FCSTD DOCUMENT  (FreeCAD 2023.521R14555 (Git shallow))
Label: Lens_asm
License: All rights reserved
objects: App::Link×4, App::DocumentObjectGroup×3, PartDesign::CoordinateSystem×1, App::FeaturePython×1, App::Part×1
note: 1 computed .brp shape members not serialized (recipe doc carries the construction recipe); baked Part::Feature solids carry a one-line shape summary decoded from their .brp
EXTERNAL_REF file=Lens_mount.FCStd obj=Local_CS
EXTERNAL_REF file=Lens_mount.FCStd obj=Part
EXTERNAL_REF file=Lens_clamp.FCStd obj=Local_CS
EXTERNAL_REF file=Lens_mount.FCStd obj=Local_CS001
EXTERNAL_REF file=Lens_clamp.FCStd obj=Part
EXTERNAL_REF file=Light_mount.FCStd obj=LCS_0
EXTERNAL_REF file=Light_mount.FCStd obj=Light_mount
EXTERNAL_REF file=Lens_Filter.FCStd obj=Local_CS
EXTERNAL_REF file=Light_mount.FCStd obj=Local_CS
EXTERNAL_REF file=Lens_Filter.FCStd obj=Part

FEATURE [App::DocumentObjectGroup] Parts
  ClaimAllChildren = true
  ExportMode = 1
  TreeRank = 12
  _GroupVersion = 1
FEATURE [PartDesign::CoordinateSystem] LCS_Origin
  AttacherType = Attacher::AttachEngine3D
  AttachmentSupport = -> [X_Axis]
  InvalidShape = false
  MapMode = 2
  Support = -> [X_Axis]
  TreeRank = 4
  ValidateShape = false
FEATURE [App::DocumentObjectGroup] Constraints
  ClaimAllChildren = true
  ExportMode = 1
  TreeRank = 11
  _GroupVersion = 1
FEATURE [App::FeaturePython] Variables  # WARN: FeaturePython — macro-defined, semantics opaque (R4)
  TreeRank = 17
  Type = App::PropertyContainer
FEATURE [App::DocumentObjectGroup] Configurations
  ClaimAllChildren = true
  ExportMode = 1
  TreeRank = 18
  _GroupVersion = 1
FEATURE [App::Link] Mount  label="Mount(Mount)"
  AttachedBy = #Local_CS
  AttachedTo = Parent Assembly#LCS_Origin
  AutoLinkLabel = true
  AutoPlacement = true
  LinkedObject = -> <external Lens_mount.FCStd>#Part
  SolverId = Asm4EE
  SyncGroupVisibility = false
  TreeRank = 19
  _LinkVersion = 1
  expr: Placement = LCS_Origin.Placement * AttachmentOffset * Lens_mount#Local_CS.Placement ^ (-1)
FEATURE [App::Link] Clamp  label="Clamp(Clamp)"
  AttachedBy = #Local_CS
  AttachedTo = Mount#Local_CS001
  AutoLinkLabel = true
  AutoPlacement = true
  LinkPlacement = pos=(9.2457e-12,0.0015863,67) rot=(0,0,1;4.71239rad)
  LinkedObject = -> <external Lens_clamp.FCStd>#Part
  Placement = pos=(9.2457e-12,0.0015863,67) rot=(0,0,1;4.71239rad)
  SolverId = Asm4EE
  SyncGroupVisibility = false
  TreeRank = 20
  _LinkVersion = 1
  expr: Placement = Mount.Placement * Lens_mount#Local_CS001.Placement * AttachmentOffset * Lens_clamp#Local_CS.Placement ^ (-1)
FEATURE [App::Link] Light_mount  label="Light_mount(Light_mount)"
  AttachedBy = #LCS_0
  AttachedTo = Mount#Local_CS001
  AttachmentOffset = pos=(0,0,0) rot=(0,0,1;3.14159rad)
  AutoLinkLabel = true
  AutoPlacement = true
  LinkPlacement = pos=(9.2452e-12,0.0015863,65) rot=(0,0,1;0rad)
  LinkedObject = -> <external Light_mount.FCStd>#Light_mount
  Placement = pos=(9.2452e-12,0.0015863,65) rot=(0,0,1;0rad)
  SolverId = Asm4EE
  SyncGroupVisibility = false
  TreeRank = 21
  _LinkVersion = 1
  expr: Placement = Mount.Placement * Lens_mount#Local_CS001.Placement * AttachmentOffset * Light_mount#LCS_0.Placement ^ (-1)
FEATURE [App::Link] Filter001  label="Filter001(Filter001)"
  AttachedBy = #Local_CS
  AttachedTo = Light_mount#Local_CS
  AttachmentOffset = pos=(0,0,0) rot=(0,0,1;4.71239rad)
  AutoLinkLabel = true
  AutoPlacement = true
  LinkPlacement = pos=(9.251e-12,-64.9984,87.5) rot=(0,0,1;0rad)
  LinkedObject = -> <external Lens_Filter.FCStd>#Part
  Placement = pos=(9.251e-12,-64.9984,87.5) rot=(0,0,1;0rad)
  SolverId = Asm4EE
  SyncGroupVisibility = false
  TreeRank = 22
  _LinkVersion = 1
  expr: Placement = Light_mount.Placement * Light_mount#Local_CS.Placement * AttachmentOffset * Lens_Filter#Local_CS.Placement ^ (-1)
FEATURE [App::Part] Assembly
  AssemblyType = Part::Link
  ClaimAllChildren = false
  ExportMode = 1
  Group = -> [LCS_Origin,Constraints,Variables,Configurations,Mount,Clamp,Light_mount,Filter001]
  Origin = -> Origin
  TreeRank = 14
  Type = Assembly
  _ExportChildren = -> [LCS_Origin,Constraints,Variables,Configurations,Mount,Clamp,Light_mount,Filter001]
  _GroupVersion = 1

RESOLVED EXTERNAL PARTS (link-assembly join: the EXTERNAL_REF files above that resolve inside this repo's crawl, each included once):
---- part Lens_Filter.FCStd = doc fcstd_d97ffb5e31ca ----
FCSTD DOCUMENT  (FreeCAD 2023.521R14555 (Git shallow))
Label: Lens_Filter
License: All rights reserved
objects: Sketcher::SketchObject×4, PartDesign::Pad×2, PartDesign::Pocket×2, PartDesign::Chamfer×1, PartDesign::Body×1, PartDesign::CoordinateSystem×1, App::Part×1
note: 25 computed .brp shape members not serialized (recipe doc carries the construction recipe); baked Part::Feature solids carry a one-line shape summary decoded from their .brp

FEATURE [Sketcher::SketchObject] Sketch
  ArcFitTolerance = 1e-06
  AttachmentSupport = -> [XZ_Plane]
  ExternalBSplineMaxDegree = 5
  ExternalBSplineTolerance = 0.0001
  FullyConstrained = true
  InternalTolerance = 1e-06
  InvalidShape = false
  MakeInternals = false
  MapMode = 5
  Placement = pos=(0,0,0) rot=(1,0,0;1.5708rad)
  Support = -> [XZ_Plane]
  TreeRank = 14
  ValidateShape = false
  sketch-geometry (5):
    g0: LineSegment StartX=-44.5 StartY=-2.25 StartZ=0 EndX=-44.5 EndY=2.25 EndZ=0
    g1: LineSegment StartX=-44.5 StartY=2.25 StartZ=0 EndX=44.5 EndY=2.25 EndZ=0
    g2: LineSegment StartX=44.5 StartY=2.25 StartZ=0 EndX=44.5 EndY=-2.25 EndZ=0
    g3: LineSegment StartX=44.5 StartY=-2.25 StartZ=0 EndX=-44.5 EndY=-2.25 EndZ=0
    g4: GeomPoint [constr] X=0 Y=0 Z=0
  constraints (12):
    c: Coincident(g0,g1)
    c: Coincident(g1,g2)
    c: Coincident(g2,g3)
    c: Coincident(g3,g0)
    c: Horizontal(g1)
    c: Horizontal(g3)
    c: Vertical(g0)
    c: Vertical(g2)
    c: Symmetric(g1,g0,g4)
    c: Coincident(g4,g-1)
    c: DistanceX(g1,g1) = 89
    c: DistanceY(g2,g2) = 4.5
FEATURE [PartDesign::Pad] Pad
  AddSubType = 0
  AlongSketchNormal = false
  AutoTaperInnerAngle = true
  CheckUpToFaceLimits = true
  ClaimChildren = false
  Direction = (0,-1,-2e-16)
  Fit = 0
  FitJoin = 0
  InnerFit = 0
  InnerFitJoin = 0
  InvalidShape = false
  Length = 125
  Length2 = 10
  Linearize = true
  NewSolid = false
  Profile = -> Sketch
  ReferenceAxis = -> Sketch [N_Axis]
  Reversed = true
  Suppress = false
  TaperInnerAngle = 0
  TaperInnerAngleRev = 0
  TreeRank = 15
  Type = 0
  ValidateShape = true
  _ProfileBasedVersion = 1
FEATURE [Sketcher::SketchObject] Sketch001
  ArcFitTolerance = 1e-06
  AttachmentSupport = -> [Pad]
  ExternalBSplineMaxDegree = 5
  ExternalBSplineTolerance = 0.0001
  FullyConstrained = true
  InternalTolerance = 1e-06
  InvalidShape = false
  MakeInternals = false
  MapMode = 5
  Placement = pos=(0,-5e-16,2.25) rot=(0,0,1;0rad)
  Support = -> [Pad]
  TreeRank = 16
  ValidateShape = false
  sketch-geometry (5):
    g0: LineSegment StartX=-38.25 StartY=104 StartZ=0 EndX=-38.25 EndY=27.5 EndZ=0
    g1: LineSegment StartX=-38.25 StartY=27.5 StartZ=0 EndX=38.25 EndY=27.5 EndZ=0
    g2: LineSegment StartX=38.25 StartY=27.5 StartZ=0 EndX=38.25 EndY=104 EndZ=0
    g3: LineSegment StartX=38.25 StartY=104 StartZ=0 EndX=-38.25 EndY=104 EndZ=0
    g4: GeomPoint [constr] X=0 Y=65.75 Z=0
  constraints (13):
    c: Coincident(g0,g1)
    c: Coincident(g1,g2)
    c: Coincident(g2,g3)
    c: Coincident(g3,g0)
    c: Horizontal(g1)
    c: Horizontal(g3)
    c: Vertical(g0)
    c: Vertical(g2)
    c: Symmetric(g1,g0,g4)
    c: Vertical(g4,g-1)
    c: DistanceY(g2,g2) = 76.5
    c: Equal(g2,g3)
    c: DistanceY(g-1,g0) = 27.5
FEATURE [PartDesign::Pocket] Pocket
  AddSubType = 1
  AlongSketchNormal = false
  AutoTaperInnerAngle = true
  BaseFeature = -> Pad
  CheckUpToFaceLimits = true
  ClaimChildren = false
  Direction = (0,2e-16,-1)
  Fit = 0
  FitJoin = 0
  InnerFit = 0
  InnerFitJoin = 0
  InvalidShape = false
  Length = 0
  Length2 = 10
  Linearize = true
  NewSolid = false
  Offset = -1
  Profile = -> Sketch001
  ReferenceAxis = -> Sketch001 [N_Axis]
  Suppress = false
  TaperInnerAngle = 0
  TaperInnerAngleRev = 0
  TreeRank = 17
  Type = 3
  UpToFace = -> Pad [Face4]
  ValidateShape = true
  _ProfileBasedVersion = 1
  _Version = 1
FEATURE [Sketcher::SketchObject] Sketch002
  ArcFitTolerance = 1e-06
  AttachmentSupport = -> [Pocket]
  ExternalBSplineMaxDegree = 5
  ExternalBSplineTolerance = 0.0001
  ExternalGeometry = -> [Pocket]
  FullyConstrained = true
  InternalTolerance = 1e-06
  InvalidShape = false
  MakeInternals = false
  MapMode = 5
  Placement = pos=(0,3e-16,-1.25) rot=(0,0,1;0rad)
  Support = -> [Pocket]
  TreeRank = 18
  ValidateShape = false
  sketch-geometry (5):
    g0: LineSegment StartX=-35 StartY=30.75 StartZ=0 EndX=-35 EndY=100.75 EndZ=0
    g1: LineSegment StartX=-35 StartY=100.75 StartZ=0 EndX=35 EndY=100.75 EndZ=0
    g2: LineSegment StartX=35 StartY=100.75 StartZ=0 EndX=35 EndY=30.75 EndZ=0
    g3: LineSegment StartX=35 StartY=30.75 StartZ=0 EndX=-35 EndY=30.75 EndZ=0
    g4: GeomPoint [constr] X=4e-16 Y=65.75 Z=0
  constraints (12):
    c: Coincident(g0,g1)
    c: Coincident(g1,g2)
    c: Coincident(g2,g3)
    c: Coincident(g3,g0)
    c: Horizontal(g1)
    c: Horizontal(g3)
    c: Vertical(g0)
    c: Vertical(g2)
    c: Symmetric(g1,g0,g4)
    c: Symmetric(g-3,g-4,g4)
    c: Equal(g2,g1)
    c: DistanceY(g2,g2) = 70
FEATURE [PartDesign::Pocket] Pocket001
  AddSubType = 1
  AlongSketchNormal = false
  AutoTaperInnerAngle = true
  BaseFeature = -> Pocket
  CheckUpToFaceLimits = true
  ClaimChildren = false
  Direction = (0,2e-16,-1)
  Fit = 0
  FitJoin = 0
  InnerFit = 0
  InnerFitJoin = 0
  InvalidShape = false
  Length = 5
  Length2 = 10
  Linearize = true
  Midplane = true
  NewSolid = false
  Profile = -> Sketch002
  ReferenceAxis = -> Sketch002 [N_Axis]
  Suppress = false
  TaperInnerAngle = 0
  TaperInnerAngleRev = 0
  TreeRank = 19
  Type = 1
  ValidateShape = true
  _ProfileBasedVersion = 1
  _Version = 1
FEATURE [Sketcher::SketchObject] Sketch003
  ArcFitTolerance = 1e-06
  AttachmentSupport = -> [Pocket001]
  ExternalBSplineMaxDegree = 5
  ExternalBSplineTolerance = 0.0001
  ExternalGeometry = -> [Pocket001]
  FullyConstrained = true
  InternalTolerance = 1e-06
  InvalidShape = false
  MakeInternals = false
  MapMode = 5
  Placement = pos=(0,0,0) rot=(1,0,0;1.5708rad)
  Support = -> [Pocket001]
  TreeRank = 20
  ValidateShape = false
  sketch-geometry (5):
    g0: LineSegment StartX=-44.5 StartY=12.75 StartZ=0 EndX=-44.5 EndY=-2.25 EndZ=0
    g1: LineSegment StartX=-44.5 StartY=-2.25 StartZ=0 EndX=44.5 EndY=-2.25 EndZ=0
    g2: LineSegment StartX=44.5 StartY=-2.25 StartZ=0 EndX=44.5 EndY=12.75 EndZ=0
    g3: LineSegment StartX=44.5 StartY=12.75 StartZ=0 EndX=-44.5 EndY=12.75 EndZ=0
    g4: GeomPoint [constr] X=0 Y=5.25 Z=0
  constraints (12):
    c: Coincident(g0,g1)
    c: Coincident(g1,g2)
    c: Coincident(g2,g3)
    c: Coincident(g3,g0)
    c: Horizontal(g1)
    c: Horizontal(g3)
    c: Vertical(g0)
    c: Vertical(g2)
    c: Symmetric(g1,g0,g4)
    c: PointOnObject(g4,g-2)
    c: Coincident(g0,g-3)
    c: DistanceY(g2,g2) = 15
FEATURE [PartDesign::Pad] Pad001
  AddSubType = 0
  AlongSketchNormal = false
  AutoTaperInnerAngle = true
  BaseFeature = -> Pocket001
  CheckUpToFaceLimits = true
  ClaimChildren = false
  Direction = (0,-1,-2e-16)
  Fit = 0
  FitJoin = 0
  InnerFit = 0
  InnerFitJoin = 0
  InvalidShape = false
  Length = 5
  Length2 = 10
  Linearize = true
  NewSolid = false
  Profile = -> Sketch003
  ReferenceAxis = -> Sketch003 [N_Axis]
  Suppress = false
  TaperInnerAngle = 0
  TaperInnerAngleRev = 0
  TreeRank = 21
  Type = 0
  ValidateShape = true
  _ProfileBasedVersion = 1
FEATURE [PartDesign::Chamfer] Chamfer
  AddSubType = 0
  Angle = 45
  Base = -> Pad001 [Edge46,Edge45,Edge36,Edge19,Edge22,Edge47]
  BaseFeature = -> Pad001
  ChamferType = 0
  FlipDirection = false
  InvalidShape = false
  NewSolid = false
  Size = 2
  Size2 = 1
  SupportTransform = false
  Suppress = false
  TreeRank = 22
  UseAllEdges = false
  ValidateShape = true
FEATURE [PartDesign::Body] Body
  AutoGroupSolids = false
  ClaimAllChildren = false
  ExportMode = 0
  Group = -> [Sketch,Pad,Sketch001,Pocket,Sketch002,Pocket001,Sketch003,Pad001,Chamfer]
  InvalidShape = false
  Origin = -> Origin001
  Tip = -> Chamfer
  TreeRank = 13
  ValidateShape = false
  _ExportChildren = -> [Pad,Pocket,Pocket001,Pad001,Chamfer]
  _GroupVersion = 1
FEATURE [PartDesign::CoordinateSystem] Local_CS  label="Filter"
  AttacherType = Attacher::AttachEngine3D
  AttachmentSupport = -> [Chamfer]
  InvalidShape = false
  MapMode = 5
  Placement = pos=(0,125,2.78e-14) rot=(0,0.707107,0.707107;3.14159rad)
  Support = -> [Chamfer]
  TreeRank = 23
  ValidateShape = false
FEATURE [App::Part] Part  label="Filter001"
  ClaimAllChildren = false
  ExportMode = 1
  Group = -> [Body,Local_CS]
  Origin = -> Origin
  TreeRank = 3
  _ExportChildren = -> [Body,Local_CS]
  _GroupVersion = 1
---- part Lens_clamp.FCStd = doc fcstd_ed5a11fa4ce1 ----
FCSTD DOCUMENT  (FreeCAD 2023.521R14555 (Git shallow))
Label: Lens_clamp
License: All rights reserved
objects: Sketcher::SketchObject×3, PartDesign::Pad×1, PartDesign::Groove×1, PartDesign::CoordinateSystem×1, PartDesign::Pocket×1, PartDesign::Fillet×1, PartDesign::Body×1, App::Part×1
note: 20 computed .brp shape members not serialized (recipe doc carries the construction recipe); baked Part::Feature solids carry a one-line shape summary decoded from their .brp

FEATURE [Sketcher::SketchObject] Sketch
  ArcFitTolerance = 1e-06
  AttachmentSupport = -> [XY_Plane]
  ExternalBSplineMaxDegree = 5
  ExternalBSplineTolerance = 0.0001
  FullyConstrained = true
  InternalTolerance = 1e-06
  InvalidShape = false
  MakeInternals = false
  MapMode = 5
  Support = -> [XY_Plane]
  TreeRank = 12
  ValidateShape = false
  sketch-geometry (7):
    g0: Circle CenterX=-55 CenterY=55 CenterZ=0 NormalX=0 NormalY=0 NormalZ=1 AngleXU=0 Radius=2.75
    g1: Circle CenterX=55 CenterY=55 CenterZ=0 NormalX=0 NormalY=0 NormalZ=1 AngleXU=0 Radius=2.75
    g2: Circle CenterX=55 CenterY=-55 CenterZ=0 NormalX=0 NormalY=0 NormalZ=1 AngleXU=0 Radius=2.75
    g3: Circle CenterX=-55 CenterY=-55 CenterZ=0 NormalX=0 NormalY=0 NormalZ=1 AngleXU=0 Radius=2.75
    g4: Circle CenterX=0 CenterY=0 CenterZ=0 NormalX=0 NormalY=0 NormalZ=1 AngleXU=0 Radius=85
    g5: LineSegment [constr] StartX=0 StartY=0 StartZ=0 EndX=55 EndY=55 EndZ=0
    g6: LineSegment [constr] StartX=0 StartY=0 StartZ=0 EndX=55 EndY=-55 EndZ=0
  constraints (16):
    c: Equal(g2,g1)
    c: Equal(g1,g0)
    c: Equal(g0,g3)
    c: Diameter(g3) = 5.5
    c: Coincident(g4,g-1)
    c: Diameter(g4) = 170
    c: Coincident(g5,g4)
    c: Coincident(g5,g1)
    c: Coincident(g6,g4)
    c: Coincident(g6,g2)
    c: Equal(g6,g5)
    c: DistanceX(g6,g6) = 55
    c: Symmetric(g2,g0,g4)
    c: Symmetric(g3,g1,g4)
    c: Perpendicular(g5,g6)
    c: Vertical(g2,g1)
FEATURE [PartDesign::Pad] Pad
  AddSubType = 0
  AlongSketchNormal = false
  AutoTaperInnerAngle = true
  CheckUpToFaceLimits = true
  ClaimChildren = false
  Direction = (0,0,1)
  Fit = 0
  FitJoin = 0
  InnerFit = 0
  InnerFitJoin = 0
  InvalidShape = false
  Length = 20
  Length2 = 10
  Linearize = true
  NewSolid = false
  Profile = -> Sketch
  ReferenceAxis = -> Sketch [N_Axis]
  Reversed = true
  Suppress = false
  TaperInnerAngle = 0
  TaperInnerAngleRev = 0
  TreeRank = 13
  Type = 0
  ValidateShape = true
  _ProfileBasedVersion = 1
FEATURE [Sketcher::SketchObject] Sketch001
  ArcFitTolerance = 1e-06
  AttachmentSupport = -> [XZ_Plane]
  ExternalBSplineMaxDegree = 5
  ExternalBSplineTolerance = 0.0001
  ExternalGeometry = -> [Pad]
  FullyConstrained = true
  InternalTolerance = 1e-06
  InvalidShape = false
  MakeInternals = false
  MapMode = 5
  Placement = pos=(0,0,0) rot=(1,0,0;1.5708rad)
  Support = -> [XZ_Plane]
  TreeRank = 14
  ValidateShape = false
  sketch-geometry (8):
    g0: LineSegment StartX=-70 StartY=-2 StartZ=0 EndX=-85 EndY=-2 EndZ=0
    g1: LineSegment StartX=-85 StartY=-2 StartZ=0 EndX=-85 EndY=-20 EndZ=0
    g2: LineSegment StartX=-85 StartY=-20 StartZ=0 EndX=0 EndY=-20 EndZ=0
    g3: LineSegment StartX=0 StartY=-20 StartZ=0 EndX=0 EndY=0 EndZ=0
    g4: LineSegment StartX=0 StartY=0 StartZ=0 EndX=-65.8 EndY=0 EndZ=0
    g5: LineSegment StartX=-61 StartY=-12 StartZ=0 EndX=-55 EndY=-12 EndZ=0
    g6: LineSegment StartX=-70 StartY=-2 StartZ=0 EndX=-61 EndY=-12 EndZ=0
    g7: LineSegment StartX=-55 StartY=-12 StartZ=0 EndX=-65.8 EndY=0 EndZ=0
  constraints (22):
    c: Horizontal(g0)
    c: Coincident(g1,g0)
    c: Vertical(g1)
    c: Coincident(g2,g1)
    c: Coincident(g1,g-4)
    c: DistanceY(g0,g-3) = 2
    c: Horizontal(g4)
    c: Vertical(g3)
    c: Coincident(g3,g-1)
    c: Coincident(g3,g4)
    c: DistanceX(g5,g3) = 55
    c: Coincident(g2,g3)
    c: Horizontal(g2)
    c: Horizontal(g5)
    c: DistanceX(g5,g5) = 6
    c: Coincident(g6,g0)
    c: Coincident(g6,g5)
    c: Coincident(g7,g5)
    c: Coincident(g7,g4)
    c: DistanceY(g5,g0) = 10
    c: DistanceX(g0,g2) = 70
    c: Parallel(g6,g7)
FEATURE [PartDesign::Groove] Groove
  AddSubType = 1
  Angle = 360
  Axis = (0,-2e-16,1)
  Base = (0,0,0)
  BaseFeature = -> Pad
  ClaimChildren = false
  Fit = 0
  FitJoin = 0
  InnerFit = 0
  InnerFitJoin = 0
  InvalidShape = false
  Linearize = true
  NewSolid = false
  Profile = -> Sketch001
  ReferenceAxis = -> Sketch001 [V_Axis]
  Reversed = true
  Suppress = false
  TreeRank = 15
  ValidateShape = true
  _ProfileBasedVersion = 1
FEATURE [PartDesign::CoordinateSystem] Local_CS  label="Center"
  AttacherType = Attacher::AttachEngine3D
  AttachmentSupport = -> [Groove]
  InvalidShape = false
  MapMode = 11
  Placement = pos=(0,4e-16,-2) rot=(0,0,-1;1.5708rad)
  Support = -> [Groove]
  TreeRank = 19
  ValidateShape = false
FEATURE [Sketcher::SketchObject] Sketch002
  ArcFitTolerance = 1e-06
  AttachmentSupport = -> [Groove]
  ExternalBSplineMaxDegree = 5
  ExternalBSplineTolerance = 0.0001
  ExternalGeometry = -> [Groove]
  FullyConstrained = true
  InternalTolerance = 1e-06
  InvalidShape = false
  MakeInternals = false
  MapMode = 5
  Support = -> [Groove]
  TreeRank = 20
  ValidateShape = false
  sketch-geometry (13):
    g0: LineSegment StartX=-60 StartY=-55 StartZ=0 EndX=-60 EndY=55 EndZ=0
    g1: LineSegment StartX=-55 StartY=60 StartZ=0 EndX=55 EndY=60 EndZ=0
    g2: LineSegment StartX=60 StartY=55 StartZ=0 EndX=60 EndY=-55 EndZ=0
    g3: LineSegment StartX=55 StartY=-60 StartZ=0 EndX=-55 EndY=-60 EndZ=0
    g4: GeomPoint [constr] X=0 Y=0 Z=0
    g5: ArcOfCircle CenterX=55 CenterY=55 CenterZ=0 NormalX=0 NormalY=0 NormalZ=1 AngleXU=0 Radius=5 StartAngle=-9e-16 EndAngle=1.5708
    g6: GeomPoint [constr] X=60 Y=60 Z=0
    g7: ArcOfCircle CenterX=-55 CenterY=55 CenterZ=0 NormalX=0 NormalY=0 NormalZ=1 AngleXU=0 Radius=5 StartAngle=1.5708 EndAngle=3.14159
    g8: GeomPoint [constr] X=-60 Y=60 Z=0
    g9: ArcOfCircle CenterX=-55 CenterY=-55 CenterZ=0 NormalX=0 NormalY=0 NormalZ=1 AngleXU=0 Radius=5 StartAngle=3.14159 EndAngle=4.71239
    g10: GeomPoint [constr] X=-60 Y=-60 Z=0
    g11: ArcOfCircle CenterX=55 CenterY=-55 CenterZ=0 NormalX=0 NormalY=0 NormalZ=1 AngleXU=0 Radius=5 StartAngle=4.71239 EndAngle=6.28319
    g12: GeomPoint [constr] X=60 Y=-60 Z=0
  constraints (26):
    c: Horizontal(g1)
    c: Horizontal(g3)
    c: Vertical(g0)
    c: Vertical(g2)
    c: Symmetric(g6,g10,g4)
    c: Coincident(g4,g-1)
    c: DistanceX(g8,g6) = 120
    c: PointOnObject(g6,g1)
    c: PointOnObject(g6,g2)
    c: Tangent(g1,g5) = 1.5708
    c: Tangent(g2,g5) = 1.5708
    c: PointOnObject(g8,g1)
    c: PointOnObject(g8,g0)
    c: Tangent(g1,g7) = 1.5708
    c: Tangent(g0,g7) = 1.5708
    c: PointOnObject(g10,g3)
    c: Tangent(g0,g9) = 1.5708
    c: Tangent(g3,g9) = 1.5708
    c: PointOnObject(g12,g3)
    c: PointOnObject(g12,g2)
    c: Tangent(g3,g11) = 1.5708
    c: Tangent(g2,g11) = 1.5708
    c: Equal(g3,g2)
    c: Equal(g2,g0)
    c: Coincident(g9,g-5)
    c: Coincident(g11,g-4)
FEATURE [PartDesign::Pocket] Pocket
  AddSubType = 2
  AlongSketchNormal = false
  AutoTaperInnerAngle = true
  BaseFeature = -> Groove
  CheckUpToFaceLimits = true
  ClaimChildren = false
  Direction = (0,0,-1)
  Fit = 0
  FitJoin = 0
  InnerFit = 0
  InnerFitJoin = 0
  InvalidShape = false
  Length = 5
  Length2 = 10
  Linearize = true
  NewSolid = false
  Profile = -> Sketch002
  ReferenceAxis = -> Sketch002 [N_Axis]
  Suppress = false
  TaperInnerAngle = 0
  TaperInnerAngleRev = 0
  TreeRank = 21
  Type = 1
  ValidateShape = true
  _ProfileBasedVersion = 1
  _Version = 1
FEATURE [PartDesign::Fillet] Fillet
  AddSubType = 0
  Base = -> Pocket [Edge15]
  BaseFeature = -> Pocket
  InvalidShape = false
  NewSolid = false
  Radius = 0.5
  SupportTransform = false
  Suppress = false
  TreeRank = 22
  UseAllEdges = false
  ValidateShape = true
FEATURE [PartDesign::Body] Body
  AutoGroupSolids = false
  ClaimAllChildren = false
  ExportMode = 0
  Group = -> [Sketch,Pad,Sketch001,Groove,Sketch002,Pocket,Fillet]
  InvalidShape = false
  Origin = -> Origin
  Tip = -> Fillet
  TreeRank = 10
  ValidateShape = false
  _ExportChildren = -> [Pad,Groove,Pocket,Fillet]
  _GroupVersion = 1
FEATURE [App::Part] Part  label="Clamp"
  ClaimAllChildren = false
  ExportMode = 1
  Group = -> [Body,Local_CS]
  Origin = -> Origin001
  TreeRank = 18
  _ExportChildren = -> [Body,Local_CS]
  _GroupVersion = 1
---- part Lens_mount.FCStd = doc fcstd_95109d1e49fe ----
FCSTD DOCUMENT  (FreeCAD 2023.521R14555 (Git shallow))
Label: Lens_mount
License: All rights reserved
LicenseURL: http://en.wikipedia.org/wiki/All_rights_reserved
objects: Sketcher::SketchObject×11, PartDesign::Pocket×7, PartDesign::Chamfer×6, PartDesign::Fillet×4, PartDesign::Pad×3, PartDesign::CoordinateSystem×2, PartDesign::Groove×1, PartDesign::Mirrored×1, PartDesign::Body×1, Part::SubShapeBinder×1, App::Part×1
note: 92 computed .brp shape members not serialized (recipe doc carries the construction recipe); baked Part::Feature solids carry a one-line shape summary decoded from their .brp
EXTERNAL_REF file=Lens_asm.FCStd obj=Assembly

FEATURE [Sketcher::SketchObject] Sketch
  ArcFitTolerance = 0
  AttachmentSupport = -> [XY_Plane]
  ExternalBSplineMaxDegree = 0
  ExternalBSplineTolerance = 0
  FullyConstrained = true
  InternalTolerance = 1e-06
  InvalidShape = false
  MakeInternals = false
  MapMode = 5
  Support = -> [XY_Plane]
  TreeRank = 0
  ValidateShape = false
  sketch-geometry (8):
    g0: LineSegment StartX=85 StartY=85 StartZ=0 EndX=-85 EndY=85 EndZ=0
    g1: LineSegment StartX=-85 StartY=85 StartZ=0 EndX=-85 EndY=-85 EndZ=0
    g2: LineSegment StartX=-85 StartY=-85 StartZ=0 EndX=85 EndY=-85 EndZ=0
    g3: LineSegment StartX=85 StartY=-85 StartZ=0 EndX=85 EndY=85 EndZ=0
    g4: LineSegment StartX=-60 StartY=-60 StartZ=0 EndX=60 EndY=-60 EndZ=0
    g5: LineSegment StartX=60 StartY=-60 StartZ=0 EndX=60 EndY=60 EndZ=0
    g6: LineSegment StartX=60 StartY=60 StartZ=0 EndX=-60 EndY=60 EndZ=0
    g7: LineSegment StartX=-60 StartY=60 StartZ=0 EndX=-60 EndY=-60 EndZ=0
  constraints (22):
    c: Coincident(g0,g1)
    c: Coincident(g1,g2)
    c: Coincident(g2,g3)
    c: Coincident(g3,g0)
    c: Horizontal(g0)
    c: Horizontal(g2)
    c: Vertical(g1)
    c: Vertical(g3)
    c: Symmetric(g1,g0,g-1)
    c: Equal(g3,g0)
    c: DistanceX(g0,g0) = 170
    c: Coincident(g4,g5)
    c: Coincident(g5,g6)
    c: Coincident(g6,g7)
    c: Coincident(g7,g4)
    c: Horizontal(g4)
    c: Horizontal(g6)
    c: Vertical(g5)
    c: Vertical(g7)
    c: Equal(g6,g5)
    c: DistanceX(g6,g6) = 120
    c: Symmetric(g4,g5,g-1)
FEATURE [PartDesign::Pad] Pad
  AddSubType = 0
  AutoTaperInnerAngle = true
  CheckUpToFaceLimits = true
  ClaimChildren = false
  Direction = (0,0,1)
  Fit = 0
  FitJoin = 0
  InnerFit = 0
  InnerFitJoin = 0
  InvalidShape = false
  Length = 50
  Length2 = 100
  NewSolid = false
  Profile = -> Sketch
  Suppress = false
  TaperInnerAngle = 0
  TaperInnerAngleRev = 0
  TreeRank = 0
  Type = 0
  ValidateShape = true
  _ProfileBasedVersion = 0
FEATURE [PartDesign::Chamfer] Chamfer
  AddSubType = 0
  Angle = 45
  Base = -> Pad [Edge8,Edge5,Edge1,Edge2]
  BaseFeature = -> Pad
  ChamferType = 0
  FlipDirection = false
  InvalidShape = false
  NewSolid = false
  Size = 15
  Size2 = 1
  SupportTransform = false
  Suppress = false
  TreeRank = 0
  UseAllEdges = false
  ValidateShape = true
FEATURE [Sketcher::SketchObject] Sketch001
  ArcFitTolerance = 0
  AttachmentSupport = -> [Chamfer]
  ExternalBSplineMaxDegree = 0
  ExternalBSplineTolerance = 0
  ExternalGeometry = -> [Chamfer]
  FullyConstrained = true
  InternalTolerance = 1e-06
  InvalidShape = false
  MakeInternals = false
  MapMode = 5
  Placement = pos=(0,0,50) rot=(0,0,1;0rad)
  Support = -> [Chamfer]
  TreeRank = 0
  ValidateShape = false
  sketch-geometry (9):
    g0: Circle CenterX=0 CenterY=0 CenterZ=0 NormalX=0 NormalY=0 NormalZ=1 AngleXU=0 Radius=55
    g1: LineSegment StartX=-85 StartY=-70 StartZ=0 EndX=-70 EndY=-85 EndZ=0
    g2: LineSegment StartX=-70 StartY=-85 StartZ=0 EndX=70 EndY=-85 EndZ=0
    g3: LineSegment StartX=70 StartY=-85 StartZ=0 EndX=85 EndY=-70 EndZ=0
    g4: LineSegment StartX=85 StartY=-70 StartZ=0 EndX=85 EndY=70 EndZ=0
    g5: LineSegment StartX=-85 StartY=70 StartZ=0 EndX=-85 EndY=-70 EndZ=0
    g6: LineSegment StartX=-85 StartY=70 StartZ=0 EndX=-70 EndY=85 EndZ=0
    g7: LineSegment StartX=-70 StartY=85 StartZ=0 EndX=70 EndY=85 EndZ=0
    g8: LineSegment StartX=70 StartY=85 StartZ=0 EndX=85 EndY=70 EndZ=0
  constraints (18):
    c: Coincident(g0,g-1)
    c: Coincident(g1,g-8)
    c: Coincident(g1,g-8)
    c: Coincident(g2,g1)
    c: Coincident(g2,g-7)
    c: Coincident(g3,g2)
    c: Coincident(g3,g-6)
    c: Coincident(g4,g3)
    c: Coincident(g4,g-5)
    c: Coincident(g5,g1)
    c: Coincident(g6,g5)
    c: Coincident(g6,g-9)
    c: Coincident(g7,g6)
    c: Coincident(g7,g-10)
    c: Coincident(g8,g7)
    c: Coincident(g8,g4)
    c: Coincident(g-4,g5)
    c: Diameter(g0) = 110
FEATURE [PartDesign::Pad] Pad001
  AddSubType = 0
  AutoTaperInnerAngle = true
  BaseFeature = -> Chamfer
  CheckUpToFaceLimits = true
  ClaimChildren = false
  Direction = (0,0,1)
  Fit = 0
  FitJoin = 0
  InnerFit = 0
  InnerFitJoin = 0
  InvalidShape = false
  Length = 15
  Length2 = 100
  NewSolid = false
  Profile = -> Sketch001
  Suppress = false
  TaperInnerAngle = 0
  TaperInnerAngleRev = 0
  TreeRank = 0
  Type = 0
  ValidateShape = true
  _ProfileBasedVersion = 0
FEATURE [Sketcher::SketchObject] Sketch002
  ArcFitTolerance = 0
  AttachmentSupport = -> [YZ_Plane]
  ExternalBSplineMaxDegree = 0
  ExternalBSplineTolerance = 0
  ExternalGeometry = -> [Pad001]
  FullyConstrained = true
  InternalTolerance = 1e-06
  InvalidShape = false
  MakeInternals = false
  MapMode = 5
  Placement = pos=(0,0,0) rot=(0.57735,0.57735,0.57735;2.0944rad)
  Support = -> [YZ_Plane]
  TreeRank = 0
  ValidateShape = false
  sketch-geometry (3):
    g0: ArcOfCircle CenterX=-10 CenterY=136.21 CenterZ=0 NormalX=0 NormalY=0 NormalZ=1 AngleXU=0 Radius=97.2451 StartAngle=4.23137 EndAngle=5.46153
    g1: LineSegment StartX=-54.9938 StartY=50 StartZ=0 EndX=-54.9938 EndY=65 EndZ=0
    g2: LineSegment StartX=-54.9938 StartY=65 StartZ=0 EndX=56.225 EndY=65 EndZ=0
  constraints (8):
    c: DistanceX(g0,g-1) = 10
    c: DistanceY(g-1,g0) = 136.21
    c: Coincident(g0,g-3)
    c: Horizontal(g-4,g0)
    c: Coincident(g1,g0)
    c: Coincident(g1,g-4)
    c: Coincident(g2,g0)
    c: Coincident(g1,g2)
FEATURE [PartDesign::Groove] Groove
  AddSubType = 1
  Angle = 360
  Axis = (-3e-16,3e-16,1)
  Base = (0,0,0)
  BaseFeature = -> Pad001
  ClaimChildren = false
  Fit = 0
  FitJoin = 0
  InnerFit = 0
  InnerFitJoin = 0
  InvalidShape = false
  NewSolid = false
  Profile = -> Sketch002
  ReferenceAxis = -> Sketch002 [V_Axis]
  Suppress = false
  TreeRank = 0
  ValidateShape = true
  _ProfileBasedVersion = 0
FEATURE [Sketcher::SketchObject] Sketch003
  ArcFitTolerance = 0
  AttachmentSupport = -> [Groove]
  ExternalBSplineMaxDegree = 0
  ExternalBSplineTolerance = 0
  FullyConstrained = true
  InternalTolerance = 1e-06
  InvalidShape = false
  MakeInternals = false
  MapMode = 5
  Placement = pos=(0,-85,0) rot=(1,0,0;1.5708rad)
  Support = -> [Groove]
  TreeRank = 0
  ValidateShape = false
  sketch-geometry (5):
    g0: LineSegment StartX=80 StartY=15 StartZ=0 EndX=-80 EndY=15 EndZ=0
    g1: LineSegment StartX=-80 StartY=15 StartZ=0 EndX=-80 EndY=5 EndZ=0
    g2: LineSegment StartX=-80 StartY=5 StartZ=0 EndX=80 EndY=5 EndZ=0
    g3: LineSegment StartX=80 StartY=5 StartZ=0 EndX=80 EndY=15 EndZ=0
    g4: GeomPoint [constr] X=0 Y=5 Z=0
  constraints (13):
    c: Coincident(g0,g1)
    c: Coincident(g1,g2)
    c: Coincident(g2,g3)
    c: Coincident(g3,g0)
    c: Horizontal(g0)
    c: Horizontal(g2)
    c: Vertical(g1)
    c: Vertical(g3)
    c: DistanceY(g1,g1) = 10
    c: DistanceX(g2,g2) = 160
    c: Symmetric(g2,g2,g4)
    c: Vertical(g4,g-1)
    c: DistanceY(g-1,g4) = 5
FEATURE [PartDesign::Pocket] Pocket
  AddSubType = 1
  AutoTaperInnerAngle = true
  BaseFeature = -> Groove
  CheckUpToFaceLimits = true
  ClaimChildren = false
  Direction = (1,1,1)
  Fit = 0
  FitJoin = 0
  InnerFit = 0
  InnerFitJoin = 0
  InvalidShape = false
  Length = 0
  Length2 = 100
  NewSolid = false
  Offset = -14
  Profile = -> Sketch003
  Suppress = false
  TaperInnerAngle = 0
  TaperInnerAngleRev = 0
  TreeRank = 0
  Type = 3
  UpToFace = -> Groove [Face1]
  ValidateShape = true
  _ProfileBasedVersion = 0
  _Version = 0
FEATURE [Sketcher::SketchObject] Sketch004
  ArcFitTolerance = 0
  AttachmentSupport = -> [Pocket]
  ExternalBSplineMaxDegree = 0
  ExternalBSplineTolerance = 0
  FullyConstrained = true
  InternalTolerance = 1e-06
  InvalidShape = false
  MakeInternals = false
  MapMode = 5
  Placement = pos=(0,0,65) rot=(0,0,1;0rad)
  Support = -> [Pocket]
  TreeRank = 0
  ValidateShape = false
  sketch-geometry (6):
    g0: Circle CenterX=55 CenterY=55 CenterZ=0 NormalX=0 NormalY=0 NormalZ=1 AngleXU=0 Radius=3.5
    g1: Circle CenterX=55 CenterY=-55 CenterZ=0 NormalX=0 NormalY=0 NormalZ=1 AngleXU=0 Radius=3.5
    g2: Circle CenterX=-55 CenterY=-55 CenterZ=0 NormalX=0 NormalY=0 NormalZ=1 AngleXU=0 Radius=3.5
    g3: Circle CenterX=-55 CenterY=55 CenterZ=0 NormalX=0 NormalY=0 NormalZ=1 AngleXU=0 Radius=3.5
    g4: LineSegment [constr] StartX=0 StartY=0 StartZ=0 EndX=55 EndY=55 EndZ=0
    g5: LineSegment [constr] StartX=0 StartY=0 StartZ=0 EndX=55 EndY=-55 EndZ=0
  constraints (14):
    c: Equal(g3,g2)
    c: Equal(g2,g1)
    c: Equal(g1,g0)
    c: Symmetric(g0,g2,g-1)
    c: Symmetric(g1,g3,g-1)
    c: Vertical(g1,g0)
    c: Horizontal(g1,g2)
    c: Coincident(g4,g-1)
    c: Coincident(g4,g0)
    c: Coincident(g5,g4)
    c: Coincident(g5,g1)
    c: Perpendicular(g4,g5)
    c: DistanceX(g5,g5) = 55
    c: Diameter(g1) = 7
FEATURE [PartDesign::Pocket] Pocket001
  AddSubType = 1
  AutoTaperInnerAngle = true
  BaseFeature = -> Pocket
  CheckUpToFaceLimits = true
  ClaimChildren = false
  Direction = (1,1,1)
  Fit = 0
  FitJoin = 0
  InnerFit = 0
  InnerFitJoin = 0
  InvalidShape = false
  Length = 10
  Length2 = 100
  NewSolid = false
  Profile = -> Sketch004
  Suppress = false
  TaperInnerAngle = 0
  TaperInnerAngleRev = 0
  TreeRank = 0
  Type = 0
  ValidateShape = true
  _ProfileBasedVersion = 0
  _Version = 0
FEATURE [PartDesign::Chamfer] Chamfer001
  AddSubType = 0
  Angle = 45
  Base = -> Pocket001 [Edge39,Edge31,Edge30,Edge29,Edge65]
  BaseFeature = -> Pocket001
  ChamferType = 0
  FlipDirection = false
  InvalidShape = false
  NewSolid = false
  Size = 4
  Size2 = 1
  SupportTransform = false
  Suppress = false
  TreeRank = 0
  UseAllEdges = false
  ValidateShape = true
FEATURE [PartDesign::Chamfer] Chamfer002
  AddSubType = 0
  Angle = 45
  Base = -> Pocket001 [Edge39,Edge35,Edge34,Edge36,Edge65,Edge31,Edge30,Edge29]
  BaseFeature = -> Pocket001
  ChamferType = 1
  FlipDirection = true
  InvalidShape = false
  NewSolid = false
  Size = 5
  Size2 = 3
  SupportTransform = false
  Suppress = false
  TreeRank = 0
  UseAllEdges = false
  ValidateShape = true
FEATURE [PartDesign::Chamfer] Chamfer003
  AddSubType = 0
  Angle = 45
  Base = -> Chamfer002 [Edge78,Edge57]
  BaseFeature = -> Chamfer002
  ChamferType = 0
  FlipDirection = false
  InvalidShape = false
  NewSolid = false
  Size = 2
  Size2 = 1
  SupportTransform = false
  Suppress = false
  TreeRank = 0
  UseAllEdges = false
  ValidateShape = true
FEATURE [PartDesign::Fillet] Fillet
  AddSubType = 0
  Base = -> Chamfer003 [Edge42]
  BaseFeature = -> Chamfer003
  InvalidShape = false
  NewSolid = false
  Radius = 1
  SupportTransform = false
  Suppress = false
  TreeRank = 0
  UseAllEdges = false
  ValidateShape = true
FEATURE [PartDesign::Fillet] Fillet001
  AddSubType = 0
  Base = -> Fillet [Edge21]
  BaseFeature = -> Fillet
  InvalidShape = false
  NewSolid = false
  Radius = 2
  SupportTransform = false
  Suppress = false
  TreeRank = 0
  UseAllEdges = false
  ValidateShape = true
FEATURE [Sketcher::SketchObject] Sketch005
  ArcFitTolerance = 0
  AttachmentSupport = -> [Fillet001]
  ExternalBSplineMaxDegree = 0
  ExternalBSplineTolerance = 0
  ExternalGeometry = -> [Fillet001]
  FullyConstrained = true
  InternalTolerance = 1e-06
  InvalidShape = false
  MakeInternals = false
  MapMode = 5
  Placement = pos=(0,0,65) rot=(0,0,1;0rad)
  Support = -> [Fillet001]
  TreeRank = 0
  ValidateShape = false
  sketch-geometry (4):
    g0: LineSegment StartX=-85 StartY=55 StartZ=0 EndX=-105 EndY=55 EndZ=0
    g1: LineSegment StartX=-105 StartY=55 StartZ=0 EndX=-105 EndY=15 EndZ=0
    g2: LineSegment StartX=-105 StartY=15 StartZ=0 EndX=-85 EndY=15 EndZ=0
    g3: LineSegment StartX=-85 StartY=15 StartZ=0 EndX=-85 EndY=55 EndZ=0
  constraints (12):
    c: Coincident(g0,g1)
    c: Coincident(g1,g2)
    c: Coincident(g2,g3)
    c: Coincident(g3,g0)
    c: Horizontal(g0)
    c: Horizontal(g2)
    c: Vertical(g1)
    c: Vertical(g3)
    c: Vertical(g0,g-3)
    c: DistanceX(g2,g2) = 20
    c: DistanceY(g1,g1) = 40
    c: DistanceY(g0,g-4) = 30
FEATURE [PartDesign::Pad] Pad002
  AddSubType = 0
  AutoTaperInnerAngle = true
  BaseFeature = -> Fillet001
  CheckUpToFaceLimits = true
  ClaimChildren = false
  Direction = (1,1,1)
  Fit = 0
  FitJoin = 0
  InnerFit = 0
  InnerFitJoin = 0
  InvalidShape = false
  Length = 60
  Length2 = 100
  NewSolid = false
  Profile = -> Sketch005
  Reversed = true
  Suppress = false
  TaperInnerAngle = 0
  TaperInnerAngleRev = 0
  TreeRank = 0
  Type = 3
  UpToFace = -> Fillet001 [Face38]
  ValidateShape = true
  _ProfileBasedVersion = 0
FEATURE [PartDesign::Chamfer] Chamfer004
  AddSubType = 0
  Angle = 45
  Base = -> Pad002 [Edge80,Edge33,Edge81]
  BaseFeature = -> Pad002
  ChamferType = 0
  FlipDirection = false
  InvalidShape = false
  NewSolid = false
  Size = 8
  Size2 = 1
  SupportTransform = false
  Suppress = false
  TreeRank = 0
  UseAllEdges = false
  ValidateShape = true
FEATURE [Sketcher::SketchObject] Sketch006
  ArcFitTolerance = 0
  AttachmentSupport = -> [Chamfer004]
  ExternalBSplineMaxDegree = 0
  ExternalBSplineTolerance = 0
  ExternalGeometry = -> [Chamfer004]
  FullyConstrained = false
  InternalTolerance = 1e-06
  InvalidShape = false
  MakeInternals = false
  MapMode = 5
  Placement = pos=(0,55,0) rot=(0,0.707107,0.707107;3.14159rad)
  Support = -> [Chamfer004]
  TreeRank = 0
  ValidateShape = false
  sketch-geometry (7):
    g0: Circle CenterX=95 CenterY=47.5 CenterZ=0 NormalX=0 NormalY=0 NormalZ=1 AngleXU=0 Radius=3.5
    g1: Circle CenterX=95 CenterY=32.5 CenterZ=0 NormalX=0 NormalY=0 NormalZ=1 AngleXU=0 Radius=3.5
    g2: Circle CenterX=95 CenterY=17.5 CenterZ=0 NormalX=0 NormalY=0 NormalZ=1 AngleXU=0 Radius=3.5
    g3: GeomPoint [constr] X=80.5327 Y=7.71637 Z=0
    g4: GeomPoint [constr] X=85 Y=8 Z=0
    g5: GeomPoint [constr] X=95 Y=8 Z=0
    g6: GeomPoint [constr] X=105 Y=32.5 Z=0
  constraints (13):
    c: Equal(g1,g2)
    c: Equal(g2,g0)
    c: Vertical(g2,g1)
    c: Vertical(g1,g0)
    c: Horizontal(g4,g-3)
    c: Symmetric(g4,g-3,g5)
    c: Vertical(g5,g2)
    c: Symmetric(g-3,g-4,g6)
    c: Horizontal(g1,g6)
    c: Diameter(g1) = 7
    c: DistanceY(g2,g1) = 15
    c: DistanceY(g1,g0) = 15
    c: Vertical(g4,g-5)
FEATURE [PartDesign::Pocket] Pocket002
  AddSubType = 1
  AutoTaperInnerAngle = true
  BaseFeature = -> Chamfer004
  CheckUpToFaceLimits = true
  ClaimChildren = false
  Direction = (1,1,1)
  Fit = 0
  FitJoin = 0
  InnerFit = 0
  InnerFitJoin = 0
  InvalidShape = false
  Length = 15
  Length2 = 100
  NewSolid = false
  Profile = -> Sketch006
  Suppress = false
  TaperInnerAngle = 0
  TaperInnerAngleRev = 0
  TreeRank = 0
  Type = 0
  ValidateShape = true
  _ProfileBasedVersion = 0
  _Version = 0
FEATURE [PartDesign::Fillet] Fillet002
  AddSubType = 0
  Base = -> Pocket002 [Edge13,Edge12,Edge11]
  BaseFeature = -> Pocket002
  InvalidShape = false
  NewSolid = false
  Radius = 2
  SupportTransform = false
  Suppress = false
  TreeRank = 0
  UseAllEdges = false
  ValidateShape = true
FEATURE [PartDesign::Mirrored] Mirrored
  AddSubType = 0
  BaseFeature = -> Fillet002
  CopyShape = true
  InvalidShape = false
  MirrorPlane = -> Sketch005 [V_Axis]
  NewSolid = false
  OriginalSubs = -> [Pad002,Chamfer004,Pocket002,Fillet002]
  Originals = -> [Pad002,Chamfer004,Pocket002,Fillet002]
  ParallelTransform = true
  SubTransform = true
  Suppress = false
  TreeRank = 0
  ValidateShape = true
  _Version = 0
FEATURE [PartDesign::Fillet] Fillet003
  AddSubType = 0
  Base = -> Mirrored [Edge47,Edge49,Edge48,Edge46]
  BaseFeature = -> Mirrored
  InvalidShape = false
  NewSolid = false
  Radius = 2
  SupportTransform = false
  Suppress = false
  TreeRank = 0
  UseAllEdges = false
  ValidateShape = true
FEATURE [Sketcher::SketchObject] Sketch007
  ArcFitTolerance = 0
  AttachmentSupport = -> [Fillet003]
  ExternalBSplineMaxDegree = 0
  ExternalBSplineTolerance = 0
  FullyConstrained = true
  InternalTolerance = 1e-06
  InvalidShape = false
  MakeInternals = false
  MapMode = 5
  Placement = pos=(0,0,65) rot=(0,0,1;0rad)
  Support = -> [Fillet003]
  TreeRank = 0
  ValidateShape = false
  sketch-geometry (6):
    g0: Circle CenterX=-70 CenterY=-70 CenterZ=0 NormalX=0 NormalY=0 NormalZ=1 AngleXU=0 Radius=3.5
    g1: Circle CenterX=70 CenterY=-70 CenterZ=0 NormalX=0 NormalY=0 NormalZ=1 AngleXU=0 Radius=3.5
    g2: Circle CenterX=70 CenterY=70 CenterZ=0 NormalX=0 NormalY=0 NormalZ=1 AngleXU=0 Radius=3.5
    g3: Circle CenterX=-70 CenterY=70 CenterZ=0 NormalX=0 NormalY=0 NormalZ=1 AngleXU=0 Radius=3.5
    g4: LineSegment [constr] StartX=70 StartY=-70 StartZ=0 EndX=0 EndY=0 EndZ=0
    g5: LineSegment [constr] StartX=0 StartY=0 StartZ=0 EndX=70 EndY=70 EndZ=0
  constraints (15):
    c: Equal(g0,g1)
    c: Equal(g1,g2)
    c: Equal(g2,g3)
    c: Diameter(g3) = 7
    c: Vertical(g3,g0)
    c: Horizontal(g0,g1)
    c: Vertical(g1,g2)
    c: Horizontal(g2,g3)
    c: Symmetric(g3,g1,g-1)
    c: Coincident(g4,g1)
    c: Coincident(g4,g-1)
    c: Coincident(g5,g4)
    c: Coincident(g5,g2)
    c: Perpendicular(g5,g4)
    c: DistanceX(g4,g4) = 70
FEATURE [PartDesign::Pocket] Pocket003
  AddSubType = 1
  AutoTaperInnerAngle = true
  BaseFeature = -> Fillet003
  CheckUpToFaceLimits = true
  ClaimChildren = false
  Direction = (1,1,1)
  Fit = 0
  FitJoin = 0
  InnerFit = 0
  InnerFitJoin = 0
  InvalidShape = false
  Length = 15
  Length2 = 100
  NewSolid = false
  Profile = -> Sketch007
  Suppress = false
  TaperInnerAngle = 0
  TaperInnerAngleRev = 0
  TreeRank = 0
  Type = 0
  ValidateShape = true
  _ProfileBasedVersion = 0
  _Version = 0
FEATURE [PartDesign::Chamfer] Chamfer005
  AddSubType = 0
  Angle = 45
  Base = -> Pocket003 [Edge19,Edge21,Edge15,Edge13]
  BaseFeature = -> Pocket003
  ChamferType = 0
  FlipDirection = false
  InvalidShape = false
  NewSolid = false
  Size = 1
  Size2 = 1
  SupportTransform = false
  Suppress = false
  TreeRank = 0
  UseAllEdges = false
  ValidateShape = true
FEATURE [Sketcher::SketchObject] Sketch008
  ArcFitTolerance = 0
  AttachmentSupport = -> [Chamfer005]
  ExternalBSplineMaxDegree = 0
  ExternalBSplineTolerance = 0
  ExternalGeometry = -> [Chamfer005]
  FullyConstrained = true
  InternalTolerance = 1e-06
  InvalidShape = false
  MakeInternals = false
  MapMode = 5
  Placement = pos=(0,-85,0) rot=(1,0,0;1.5708rad)
  Support = -> [Chamfer005]
  TreeRank = 0
  ValidateShape = false
  sketch-geometry (4):
    g0: LineSegment StartX=80 StartY=10 StartZ=0 EndX=-80 EndY=10 EndZ=0
    g1: LineSegment StartX=-80 StartY=10 StartZ=0 EndX=-80 EndY=-10 EndZ=0
    g2: LineSegment StartX=-80 StartY=-10 StartZ=0 EndX=80 EndY=-10 EndZ=0
    g3: LineSegment StartX=80 StartY=-10 StartZ=0 EndX=80 EndY=10 EndZ=0
  constraints (11):
    c: Coincident(g0,g1)
    c: Coincident(g1,g2)
    c: Coincident(g2,g3)
    c: Coincident(g3,g0)
    c: Horizontal(g0)
    c: Horizontal(g2)
    c: Vertical(g1)
    c: Vertical(g3)
    c: Symmetric(g-3,g-3,g0)
    c: Vertical(g-4,g0)
    c: DistanceY(g3,g3) = 20
FEATURE [PartDesign::Pocket] Pocket004
  AddSubType = 1
  AutoTaperInnerAngle = true
  BaseFeature = -> Chamfer005
  CheckUpToFaceLimits = true
  ClaimChildren = false
  Direction = (1,1,1)
  Fit = 0
  FitJoin = 0
  InnerFit = 0
  InnerFitJoin = 0
  InvalidShape = false
  Length = 0
  Length2 = 100
  NewSolid = false
  Profile = -> Sketch008
  Suppress = false
  TaperInnerAngle = 0
  TaperInnerAngleRev = 0
  TreeRank = 0
  Type = 3
  UpToFace = -> Chamfer005 [Face96]
  ValidateShape = true
  _ProfileBasedVersion = 0
  _Version = 0
FEATURE [Sketcher::SketchObject] Sketch009
  ArcFitTolerance = 0
  AttachmentSupport = -> [Pocket004]
  ExternalBSplineMaxDegree = 0
  ExternalBSplineTolerance = 0
  ExternalGeometry = -> [Pocket004]
  FullyConstrained = true
  InternalTolerance = 1e-06
  InvalidShape = false
  MakeInternals = false
  MapMode = 5
  Placement = pos=(-18.416,13.5709,0) rot=(0.813622,0.411108,0.411108;1.77561rad)
  Support = -> [Pocket004]
  TreeRank = 0
  ValidateShape = false
  sketch-geometry (4):
    g0: LineSegment StartX=-113.811 StartY=10 StartZ=0 EndX=-93.8108 EndY=10 EndZ=0
    g1: LineSegment StartX=-93.8108 StartY=10 StartZ=0 EndX=-93.8108 EndY=-5 EndZ=0
    g2: LineSegment StartX=-93.8108 StartY=-5 StartZ=0 EndX=-113.811 EndY=-5 EndZ=0
    g3: LineSegment StartX=-113.811 StartY=-5 StartZ=0 EndX=-113.811 EndY=10 EndZ=0
  constraints (11):
    c: Coincident(g0,g1)
    c: Coincident(g1,g2)
    c: Coincident(g2,g3)
    c: Coincident(g3,g0)
    c: Horizontal(g0)
    c: Horizontal(g2)
    c: Vertical(g1)
    c: Vertical(g3)
    c: DistanceY(g3,g3) = 15
    c: DistanceX(g0,g0) = 20
    c: Symmetric(g0,g0,g-3)
FEATURE [PartDesign::Pocket] Pocket005
  AddSubType = 1
  AutoTaperInnerAngle = true
  BaseFeature = -> Pocket004
  CheckUpToFaceLimits = true
  ClaimChildren = false
  Direction = (1,1,1)
  Fit = 0
  FitJoin = 0
  InnerFit = 0
  InnerFitJoin = 0
  InvalidShape = false
  Length = 5
  Length2 = 100
  NewSolid = false
  Profile = -> Sketch009
  Reversed = true
  Suppress = false
  TaperInnerAngle = 0
  TaperInnerAngleRev = 0
  TreeRank = 0
  Type = 0
  ValidateShape = true
  _ProfileBasedVersion = 0
  _Version = 0
FEATURE [Sketcher::SketchObject] Sketch010
  ArcFitTolerance = 0
  AttachmentSupport = -> [Pocket005]
  ExternalBSplineMaxDegree = 0
  ExternalBSplineTolerance = 0
  ExternalGeometry = -> [Pocket005]
  FullyConstrained = true
  InternalTolerance = 1e-06
  InvalidShape = false
  MakeInternals = false
  MapMode = 5
  Placement = pos=(18.416,13.5709,0) rot=(0.813622,-0.411108,-0.411108;1.77561rad)
  Support = -> [Pocket005]
  TreeRank = 0
  ValidateShape = false
  sketch-geometry (4):
    g0: LineSegment StartX=113.811 StartY=10 StartZ=0 EndX=93.8108 EndY=10 EndZ=0
    g1: LineSegment StartX=93.8108 StartY=10 StartZ=0 EndX=93.8108 EndY=-5 EndZ=0
    g2: LineSegment StartX=93.8108 StartY=-5 StartZ=0 EndX=113.811 EndY=-5 EndZ=0
    g3: LineSegment StartX=113.811 StartY=-5 StartZ=0 EndX=113.811 EndY=10 EndZ=0
  constraints (11):
    c: Coincident(g0,g1)
    c: Coincident(g1,g2)
    c: Coincident(g2,g3)
    c: Coincident(g3,g0)
    c: Horizontal(g0)
    c: Horizontal(g2)
    c: Vertical(g1)
    c: Vertical(g3)
    c: Symmetric(g0,g0,g-3)
    c: DistanceX(g0,g0) = 20
    c: DistanceY(g3,g3) = 15
FEATURE [PartDesign::Pocket] Pocket006
  AddSubType = 1
  AutoTaperInnerAngle = true
  BaseFeature = -> Pocket005
  CheckUpToFaceLimits = true
  ClaimChildren = false
  Direction = (1,1,1)
  Fit = 0
  FitJoin = 0
  InnerFit = 0
  InnerFitJoin = 0
  InvalidShape = false
  Length = 5
  Length2 = 100
  NewSolid = false
  Profile = -> Sketch010
  Reversed = true
  Suppress = false
  TaperInnerAngle = 0
  TaperInnerAngleRev = 0
  TreeRank = 0
  Type = 0
  ValidateShape = true
  _ProfileBasedVersion = 0
  _Version = 0
FEATURE [PartDesign::Body] Body
  AutoGroupSolids = false
  ClaimAllChildren = false
  ExportMode = 0
  Group = -> [Sketch,Pad,Chamfer,Sketch001,Pad001,Sketch002,Groove,Sketch003,Pocket,Sketch004,Pocket001,Chamfer001,Chamfer002,Chamfer003,Fillet,Fillet001,Sketch005,Pad002,Chamfer004,Sketch006,Pocket002,Fillet002,Mirrored,Fillet003,Sketch007,Pocket003,Chamfer005,Sketch008,Pocket004,Sketch009,Pocket005,Sketch010,Pocket006]
  InvalidShape = false
  Origin = -> Origin
  Tip = -> Pocket006
  TreeRank = 0
  ValidateShape = false
  _ExportChildren = -> [Pad,Chamfer,Pad001,Groove,Pocket,Pocket001,Chamfer001,Chamfer002,Chamfer003,Fillet,Fillet001,Pad002,Chamfer004,Pocket002,Fillet002,Mirrored,Fillet003,Pocket003,Chamfer005,Pocket004,Pocket005,Pocket006]
  _GroupVersion = 1
FEATURE [PartDesign::CoordinateSystem] Local_CS  label="Base"
  AttacherType = Attacher::AttachEngine3D
  AttachmentSupport = -> [Origin001]
  InvalidShape = false
  Support = -> [Origin001]
  TreeRank = 4
  ValidateShape = false
FEATURE [Part::SubShapeBinder] Binder  label="Binder(Pocket006)"
  BindCopyOnChange = 0
  BindMode = 0
  ClaimChildren = false
  Context = -> <external Lens_asm.FCStd>#Assembly [Mount.Binder.]
  EdgeTolerance = 1e-06
  FillStyle = 0
  Fuse = false
  InvalidShape = false
  MakeFace = true
  MergeEdges = true
  OffsetFill = false
  OffsetIntersection = false
  OffsetJoinType = 0
  OffsetOpenResult = false
  Outline = false
  PartialLoad = false
  Relative = true
  SplitEdges = false
  Support = -> [Body[Pocket006.]]
  TightBound = false
  TreeRank = 20
  ValidateShape = false
  _Version = 8
FEATURE [PartDesign::CoordinateSystem] Local_CS001  label="Center"
  AttacherType = Attacher::AttachEngine3D
  AttachmentSupport = -> [Binder]
  InvalidShape = false
  MapMode = 11
  Placement = pos=(9.2452e-12,0.0015863,65) rot=(0,0,1;3.14159rad)
  Support = -> [Binder]
  TreeRank = 19
  ValidateShape = false
FEATURE [App::Part] Part  label="Mount"
  ClaimAllChildren = false
  ExportMode = 1
  Group = -> [Body,Local_CS,Local_CS001,Binder]
  Origin = -> Origin001
  TreeRank = 3
  _ExportChildren = -> [Body,Local_CS,Local_CS001,Binder]
  _GroupVersion = 1
---- part Light_mount.FCStd = doc fcstd_9474d3565505 ----
FCSTD DOCUMENT  (FreeCAD 2023.521R14555 (Git shallow))
Label: Light_mount
License: All rights reserved
objects: Sketcher::SketchObject×5, PartDesign::Chamfer×4, PartDesign::CoordinateSystem×3, PartDesign::Pocket×3, PartDesign::Pad×2, Part::SubShapeBinder×2, PartDesign::Plane×1, PartDesign::Body×1, App::Part×1
note: 44 computed .brp shape members not serialized (recipe doc carries the construction recipe); baked Part::Feature solids carry a one-line shape summary decoded from their .brp

FEATURE [PartDesign::CoordinateSystem] LCS_0
  AttacherType = Attacher::AttachEngine3D
  AttachmentSupport = -> [X_Axis]
  InvalidShape = false
  MapMode = 2
  Support = -> [X_Axis]
  TreeRank = 3
  ValidateShape = false
FEATURE [PartDesign::CoordinateSystem] LCS_0001
  AttacherType = Attacher::AttachEngine3D
  AttachmentSupport = -> [X_Axis001]
  InvalidShape = false
  MapMode = 2
  Support = -> [X_Axis001]
  TreeRank = 21
  ValidateShape = false
FEATURE [Sketcher::SketchObject] Sketch
  ArcFitTolerance = 1e-06
  AttachmentSupport = -> [XY_Plane001]
  ExternalBSplineMaxDegree = 5
  ExternalBSplineTolerance = 0.0001
  FullyConstrained = true
  InternalTolerance = 1e-06
  InvalidShape = false
  MakeInternals = false
  MapMode = 5
  Support = -> [XY_Plane001]
  TreeRank = 23
  ValidateShape = false
  sketch-geometry (19):
    g0: LineSegment StartX=-65 StartY=-65 StartZ=0 EndX=-65 EndY=65 EndZ=0
    g1: LineSegment StartX=-65 StartY=65 StartZ=0 EndX=65 EndY=65 EndZ=0
    g2: LineSegment StartX=65 StartY=65 StartZ=0 EndX=65 EndY=-65 EndZ=0
    g3: LineSegment StartX=65 StartY=-65 StartZ=0 EndX=-65 EndY=-65 EndZ=0
    g4: GeomPoint [constr] X=0 Y=0 Z=0
    g5: LineSegment [constr] StartX=-70 StartY=-70 StartZ=0 EndX=-70 EndY=70 EndZ=0
    g6: LineSegment [constr] StartX=-70 StartY=70 StartZ=0 EndX=70 EndY=70 EndZ=0
    g7: LineSegment [constr] StartX=70 StartY=70 StartZ=0 EndX=70 EndY=-70 EndZ=0
    g8: LineSegment [constr] StartX=70 StartY=-70 StartZ=0 EndX=-70 EndY=-70 EndZ=0
    g9: GeomPoint [constr] X=0 Y=0 Z=0
    g10: LineSegment StartX=-85 StartY=-85 StartZ=0 EndX=-85 EndY=85 EndZ=0
    g11: LineSegment StartX=-85 StartY=85 StartZ=0 EndX=85 EndY=85 EndZ=0
    g12: LineSegment StartX=85 StartY=85 StartZ=0 EndX=85 EndY=-85 EndZ=0
    g13: LineSegment StartX=85 StartY=-85 StartZ=0 EndX=-85 EndY=-85 EndZ=0
    g14: GeomPoint [constr] X=0 Y=0 Z=0
    g15: Circle CenterX=-70 CenterY=70 CenterZ=0 NormalX=0 NormalY=0 NormalZ=1 AngleXU=0 Radius=3
    g16: Circle CenterX=-70 CenterY=-70 CenterZ=0 NormalX=0 NormalY=0 NormalZ=1 AngleXU=0 Radius=3
    g17: Circle CenterX=70 CenterY=-70 CenterZ=0 NormalX=0 NormalY=0 NormalZ=1 AngleXU=0 Radius=3
    g18: Circle CenterX=70 CenterY=70 CenterZ=0 NormalX=0 NormalY=0 NormalZ=1 AngleXU=0 Radius=3
  constraints (44):
    c: Coincident(g0,g1)
    c: Coincident(g1,g2)
    c: Coincident(g2,g3)
    c: Coincident(g3,g0)
    c: Horizontal(g1)
    c: Horizontal(g3)
    c: Vertical(g0)
    c: Vertical(g2)
    c: Symmetric(g1,g0,g4)
    c: Coincident(g4,g-1)
    c: Coincident(g5,g6)
    c: Coincident(g6,g7)
    c: Coincident(g7,g8)
    c: Coincident(g8,g5)
    c: Horizontal(g6)
    c: Horizontal(g8)
    c: Vertical(g5)
    c: Vertical(g7)
    c: Symmetric(g6,g5,g9)
    c: Coincident(g9,g4)
    c: Coincident(g10,g11)
    c: Coincident(g11,g12)
    c: Coincident(g12,g13)
    c: Coincident(g13,g10)
    c: Horizontal(g11)
    c: Horizontal(g13)
    c: Vertical(g10)
    c: Vertical(g12)
    c: Symmetric(g11,g10,g14)
    c: Coincident(g14,g4)
    c: Equal(g1,g0)
    c: Equal(g6,g5)
    c: Equal(g11,g10)
    c: DistanceX(g6,g6) = 140
    c: DistanceX(g11,g11) = 170
    c: DistanceX(g1,g1) = 130
    c: Coincident(g15,g5)
    c: Coincident(g16,g5)
    c: Coincident(g17,g7)
    c: Coincident(g18,g6)
    c: Equal(g17,g18)
    c: Equal(g18,g16)
    c: Equal(g16,g15)
    c: Diameter(g15) = 6
FEATURE [PartDesign::Pad] Pad
  AddSubType = 0
  AlongSketchNormal = false
  AutoTaperInnerAngle = true
  CheckUpToFaceLimits = true
  ClaimChildren = false
  Direction = (0,0,1)
  Fit = 0
  FitJoin = 0
  InnerFit = 0
  InnerFitJoin = 0
  InvalidShape = false
  Length = 20
  Length2 = 10
  Linearize = true
  NewSolid = false
  Profile = -> Sketch
  ReferenceAxis = -> Sketch [N_Axis]
  Suppress = false
  TaperInnerAngle = 0
  TaperInnerAngleRev = 0
  TreeRank = 24
  Type = 0
  ValidateShape = true
  _ProfileBasedVersion = 1
FEATURE [Part::SubShapeBinder] Import  label="Import(XY_Plane)"
  BindCopyOnChange = 0
  BindMode = 0
  ClaimChildren = false
  Context = -> Light_mount [Body.Import.]
  EdgeTolerance = 1e-06
  FillStyle = 0
  Fuse = false
  InvalidShape = false
  MakeFace = false
  MergeEdges = true
  OffsetFill = false
  OffsetIntersection = false
  OffsetJoinType = 0
  OffsetOpenResult = false
  Outline = false
  PartialLoad = false
  Relative = true
  SplitEdges = false
  Support = -> [XY_Plane]
  TightBound = false
  TreeRank = 28
  ValidateShape = false
  _Version = 8
FEATURE [PartDesign::Plane] DatumPlane
  AttachmentOffset = pos=(0,0,10) rot=(0,0,1;0rad)
  AttachmentSupport = -> [Import]
  InvalidShape = false
  Length = 10
  MapMode = 5
  MinimumLength = 10
  MinimumWidth = 10
  Placement = pos=(0,0,10) rot=(0,0,1;0rad)
  ResizeMode = 0
  Support = -> [Import]
  TreeRank = 27
  ValidateShape = false
  Width = 10
FEATURE [Sketcher::SketchObject] Sketch001
  ArcFitTolerance = 1e-06
  AttachmentSupport = -> [DatumPlane]
  ExternalBSplineMaxDegree = 5
  ExternalBSplineTolerance = 0.0001
  ExternalGeometry = -> [Pad]
  FullyConstrained = true
  InternalTolerance = 1e-06
  InvalidShape = false
  MakeInternals = false
  MapMode = 5
  Placement = pos=(0,0,10) rot=(0,0,1;0rad)
  Support = -> [DatumPlane]
  TreeRank = 29
  ValidateShape = false
  sketch-geometry (10):
    g0: LineSegment StartX=-65 StartY=-65 StartZ=0 EndX=-65 EndY=65 EndZ=0
    g1: LineSegment StartX=-65 StartY=65 StartZ=0 EndX=65 EndY=65 EndZ=0
    g2: LineSegment StartX=65 StartY=65 StartZ=0 EndX=65 EndY=-65 EndZ=0
    g3: LineSegment StartX=65 StartY=-65 StartZ=0 EndX=-65 EndY=-65 EndZ=0
    g4: GeomPoint [constr] X=6e-16 Y=-2e-16 Z=0
    g5: LineSegment StartX=-37.5 StartY=-37.5 StartZ=0 EndX=-37.5 EndY=37.5 EndZ=0
    g6: LineSegment StartX=-37.5 StartY=37.5 StartZ=0 EndX=37.5 EndY=37.5 EndZ=0
    g7: LineSegment StartX=37.5 StartY=37.5 StartZ=0 EndX=37.5 EndY=-37.5 EndZ=0
    g8: LineSegment StartX=37.5 StartY=-37.5 StartZ=0 EndX=-37.5 EndY=-37.5 EndZ=0
    g9: GeomPoint [constr] X=6e-16 Y=-2e-16 Z=0
  constraints (23):
    c: Coincident(g0,g1)
    c: Coincident(g1,g2)
    c: Coincident(g2,g3)
    c: Coincident(g3,g0)
    c: Horizontal(g1)
    c: Horizontal(g3)
    c: Vertical(g0)
    c: Vertical(g2)
    c: Symmetric(g1,g0,g4)
    c: Coincident(g4,g-1)
    c: Coincident(g5,g6)
    c: Coincident(g6,g7)
    c: Coincident(g7,g8)
    c: Coincident(g8,g5)
    c: Horizontal(g6)
    c: Horizontal(g8)
    c: Vertical(g5)
    c: Vertical(g7)
    c: Symmetric(g6,g5,g9)
    c: Coincident(g1,g-3)
    c: DistanceX(g6,g6) = 75
    c: Coincident(g4,g9)
    c: Equal(g6,g7)
FEATURE [PartDesign::Pad] Pad001
  AddSubType = 0
  AlongSketchNormal = false
  AutoTaperInnerAngle = true
  BaseFeature = -> Pad
  CheckUpToFaceLimits = true
  ClaimChildren = false
  Direction = (0,0,1)
  Fit = 0
  FitJoin = 0
  InnerFit = 0
  InnerFitJoin = 0
  InvalidShape = false
  Length = 10
  Length2 = 10
  Linearize = true
  NewSolid = false
  Offset = 10
  Profile = -> Sketch001
  ReferenceAxis = -> Sketch001 [N_Axis]
  Reversed = true
  Suppress = false
  TaperInnerAngle = 0
  TaperInnerAngleRev = 0
  TreeRank = 30
  Type = 3
  UpToFace = -> Pad [Face14]
  ValidateShape = true
  _ProfileBasedVersion = 1
FEATURE [Sketcher::SketchObject] Sketch002
  ArcFitTolerance = 1e-06
  AttachmentSupport = -> [Pad001]
  ExternalBSplineMaxDegree = 5
  ExternalBSplineTolerance = 0.0001
  ExternalGeometry = -> [Pad001]
  FullyConstrained = true
  InternalTolerance = 1e-06
  InvalidShape = false
  MakeInternals = false
  MapMode = 5
  Placement = pos=(0,-65,0) rot=(1,0,0;1.5708rad)
  Support = -> [Pad001]
  TreeRank = 31
  ValidateShape = false
  sketch-geometry (5):
    g0: LineSegment StartX=-45 StartY=20 StartZ=0 EndX=-45 EndY=25 EndZ=0
    g1: LineSegment StartX=-45 StartY=25 StartZ=0 EndX=45 EndY=25 EndZ=0
    g2: LineSegment StartX=45 StartY=25 StartZ=0 EndX=45 EndY=20 EndZ=0
    g3: LineSegment StartX=45 StartY=20 StartZ=0 EndX=-45 EndY=20 EndZ=0
    g4: GeomPoint [constr] X=0 Y=22.5 Z=0
  constraints (13):
    c: Coincident(g0,g1)
    c: Coincident(g1,g2)
    c: Coincident(g2,g3)
    c: Coincident(g3,g0)
    c: Horizontal(g1)
    c: Horizontal(g3)
    c: Vertical(g0)
    c: Vertical(g2)
    c: Symmetric(g1,g0,g4)
    c: Vertical(g4,g-1)
    c: Horizontal(g0,g-3)
    c: DistanceX(g1,g1) = 90
    c: DistanceY(g2,g2) = 5
FEATURE [PartDesign::Pocket] Pocket
  AddSubType = 1
  AlongSketchNormal = false
  AutoTaperInnerAngle = true
  BaseFeature = -> Pad001
  CheckUpToFaceLimits = true
  ClaimChildren = false
  Direction = (0,1,-2e-16)
  Fit = 0
  FitJoin = 0
  InnerFit = 0
  InnerFitJoin = 0
  InvalidShape = false
  Length = 0
  Length2 = 10
  Linearize = true
  NewSolid = false
  Offset = -5
  Profile = -> Sketch002
  ReferenceAxis = -> Sketch002 [N_Axis]
  Refine = true
  Suppress = false
  TaperInnerAngle = 0
  TaperInnerAngleRev = 0
  TreeRank = 32
  Type = 3
  UpToFace = -> Pad001 [Face16]
  ValidateShape = true
  _ProfileBasedVersion = 1
  _Version = 1
FEATURE [PartDesign::Chamfer] Chamfer
  AddSubType = 0
  Angle = 45
  Base = -> Pocket [Edge5,Edge1,Edge8,Edge2]
  BaseFeature = -> Pocket
  ChamferType = 0
  FlipDirection = false
  InvalidShape = false
  NewSolid = false
  Size = 15
  Size2 = 1
  SupportTransform = false
  Suppress = false
  TreeRank = 33
  UseAllEdges = false
  ValidateShape = true
FEATURE [PartDesign::Chamfer] Chamfer001
  AddSubType = 0
  Angle = 45
  Base = -> Chamfer [Edge26,Edge24,Edge21,Edge4,Edge23,Edge25,Edge27,Edge28]
  BaseFeature = -> Chamfer
  ChamferType = 0
  FlipDirection = false
  InvalidShape = false
  NewSolid = false
  Size = 7
  Size2 = 1
  SupportTransform = false
  Suppress = false
  TreeRank = 34
  UseAllEdges = false
  ValidateShape = true
FEATURE [PartDesign::Chamfer] Chamfer002
  AddSubType = 0
  Angle = 45
  Base = -> Chamfer001 [Edge98,Edge96,Edge93,Edge100]
  BaseFeature = -> Chamfer001
  ChamferType = 0
  FlipDirection = false
  InvalidShape = false
  NewSolid = false
  Size = 8
  Size2 = 1
  SupportTransform = false
  Suppress = false
  TreeRank = 35
  UseAllEdges = false
  ValidateShape = true
FEATURE [Sketcher::SketchObject] Sketch003
  ArcFitTolerance = 1e-06
  AttachmentSupport = -> [Chamfer002]
  ExternalBSplineMaxDegree = 5
  ExternalBSplineTolerance = 0.0001
  ExternalGeometry = -> [Chamfer002]
  FullyConstrained = true
  InternalTolerance = 1e-06
  InvalidShape = false
  MakeInternals = false
  MapMode = 5
  Placement = pos=(0,0,20) rot=(0,0,1;0rad)
  Support = -> [Chamfer002]
  TreeRank = 36
  ValidateShape = false
  sketch-geometry (4):
    g0: Circle CenterX=-70 CenterY=70 CenterZ=0 NormalX=0 NormalY=0 NormalZ=1 AngleXU=0 Radius=5
    g1: Circle CenterX=-70 CenterY=-70 CenterZ=0 NormalX=0 NormalY=0 NormalZ=1 AngleXU=0 Radius=5
    g2: Circle CenterX=70 CenterY=-70 CenterZ=0 NormalX=0 NormalY=0 NormalZ=1 AngleXU=0 Radius=5
    g3: Circle CenterX=70 CenterY=70 CenterZ=0 NormalX=0 NormalY=0 NormalZ=1 AngleXU=0 Radius=5
  constraints (8):
    c: Coincident(g1,g-4)
    c: Coincident(g2,g-5)
    c: Coincident(g3,g-6)
    c: Coincident(g0,g-3)
    c: Equal(g0,g1)
    c: Equal(g1,g3)
    c: Equal(g3,g2)
    c: Diameter(g2) = 10
FEATURE [PartDesign::Pocket] Pocket001
  AddSubType = 1
  AlongSketchNormal = false
  AutoTaperInnerAngle = true
  BaseFeature = -> Chamfer002
  CheckUpToFaceLimits = true
  ClaimChildren = false
  Direction = (0,0,-1)
  Fit = 0
  FitJoin = 0
  InnerFit = 0
  InnerFitJoin = 0
  InvalidShape = false
  Length = 5
  Length2 = 10
  Linearize = true
  NewSolid = false
  Offset = 18
  Profile = -> Sketch003
  ReferenceAxis = -> Sketch003 [N_Axis]
  Suppress = false
  TaperInnerAngle = 0
  TaperInnerAngleRev = 0
  TreeRank = 37
  Type = 0
  ValidateShape = true
  _ProfileBasedVersion = 1
  _Version = 1
FEATURE [Sketcher::SketchObject] Sketch004
  ArcFitTolerance = 1e-06
  AttachmentSupport = -> [Pocket001]
  ExternalBSplineMaxDegree = 5
  ExternalBSplineTolerance = 0.0001
  FullyConstrained = true
  InternalTolerance = 1e-06
  InvalidShape = false
  MakeInternals = false
  MapMode = 5
  Placement = pos=(0,0,30) rot=(0,0,1;0rad)
  Support = -> [Pocket001]
  TreeRank = 38
  ValidateShape = false
  sketch-geometry (9):
    g0: Circle CenterX=-55 CenterY=55 CenterZ=0 NormalX=0 NormalY=0 NormalZ=1 AngleXU=0 Radius=3
    g1: Circle CenterX=55 CenterY=55 CenterZ=0 NormalX=0 NormalY=0 NormalZ=1 AngleXU=0 Radius=3
    g2: Circle CenterX=55 CenterY=-55 CenterZ=0 NormalX=0 NormalY=0 NormalZ=1 AngleXU=0 Radius=3
    g3: Circle CenterX=-55 CenterY=-55 CenterZ=0 NormalX=0 NormalY=0 NormalZ=1 AngleXU=0 Radius=3
    g4: LineSegment [constr] StartX=-55 StartY=-55 StartZ=0 EndX=-55 EndY=55 EndZ=0
    g5: LineSegment [constr] StartX=-55 StartY=55 StartZ=0 EndX=55 EndY=55 EndZ=0
    g6: LineSegment [constr] StartX=55 StartY=55 StartZ=0 EndX=55 EndY=-55 EndZ=0
    g7: LineSegment [constr] StartX=55 StartY=-55 StartZ=0 EndX=-55 EndY=-55 EndZ=0
    g8: GeomPoint [constr] X=0 Y=0 Z=0
  constraints (20):
    c: Coincident(g4,g5)
    c: Coincident(g5,g6)
    c: Coincident(g6,g7)
    c: Coincident(g7,g4)
    c: Horizontal(g5)
    c: Horizontal(g7)
    c: Vertical(g4)
    c: Vertical(g6)
    c: Symmetric(g5,g4,g8)
    c: Coincident(g8,g-1)
    c: Coincident(g5,g1)
    c: Coincident(g0,g4)
    c: Coincident(g3,g4)
    c: Coincident(g2,g6)
    c: Equal(g1,g2)
    c: Equal(g2,g0)
    c: Equal(g0,g3)
    c: Diameter(g0) = 6
    c: DistanceX(g5,g5) = 110
    c: Equal(g5,g6)
FEATURE [PartDesign::Pocket] Pocket002
  AddSubType = 1
  AlongSketchNormal = false
  AutoTaperInnerAngle = true
  BaseFeature = -> Pocket001
  CheckUpToFaceLimits = true
  ClaimChildren = false
  Direction = (0,0,-1)
  Fit = 0
  FitJoin = 0
  InnerFit = 0
  InnerFitJoin = 0
  InvalidShape = false
  Length = 12
  Length2 = 10
  Linearize = true
  NewSolid = false
  Profile = -> Sketch004
  ReferenceAxis = -> Sketch004 [N_Axis]
  Suppress = false
  TaperInnerAngle = 0
  TaperInnerAngleRev = 0
  TreeRank = 39
  Type = 0
  ValidateShape = true
  _ProfileBasedVersion = 1
  _Version = 1
FEATURE [PartDesign::Chamfer] Chamfer003
  AddSubType = 0
  Angle = 45
  Base = -> Pocket002 [Edge82,Edge90,Edge93]
  BaseFeature = -> Pocket002
  ChamferType = 0
  FlipDirection = false
  InvalidShape = false
  NewSolid = false
  Size = 4
  Size2 = 1
  SupportTransform = false
  Suppress = false
  TreeRank = 40
  UseAllEdges = false
  ValidateShape = true
FEATURE [PartDesign::Body] Body
  AutoGroupSolids = false
  ClaimAllChildren = false
  ExportMode = 0
  Group = -> [LCS_0001,Sketch,Pad,DatumPlane,Import,Sketch001,Pad001,Sketch002,Pocket,Chamfer,Chamfer001,Chamfer002,Sketch003,Pocket001,Sketch004,Pocket002,Chamfer003]
  InvalidShape = false
  Origin = -> Origin001
  Tip = -> Chamfer003
  TreeRank = 22
  ValidateShape = false
  _ExportChildren = -> [LCS_0001,Pad,DatumPlane,Import,Pad001,Pocket,Chamfer,Chamfer001,Chamfer002,Pocket001,Pocket002,Chamfer003]
  _GroupVersion = 1
FEATURE [Part::SubShapeBinder] Import001  label="Import001(Chamfer003)"
  BindCopyOnChange = 0
  BindMode = 0
  ClaimChildren = false
  EdgeTolerance = 1e-06
  FillStyle = 0
  Fuse = false
  InvalidShape = false
  MakeFace = false
  MergeEdges = true
  OffsetFill = false
  OffsetIntersection = false
  OffsetJoinType = 0
  OffsetOpenResult = false
  Outline = false
  PartialLoad = false
  Relative = true
  SplitEdges = false
  Support = -> [Body[Chamfer003.]]
  TightBound = false
  TreeRank = 44
  ValidateShape = false
  _Version = 8
FEATURE [PartDesign::CoordinateSystem] Local_CS  label="Filter"
  AttacherType = Attacher::AttachEngine3D
  AttachmentSupport = -> [Import001]
  InvalidShape = false
  MapMode = 45
  Placement = pos=(4e-16,60,22.5) rot=(0.57735,0.57735,0.57735;4.18879rad)
  Support = -> [Import001]
  TreeRank = 43
  ValidateShape = false
FEATURE [App::Part] Light_mount
  ClaimAllChildren = false
  ExportMode = 1
  Group = -> [LCS_0,Body,Local_CS]
  Origin = -> Origin
  TreeRank = 11
  _ExportChildren = -> [LCS_0,Body,Local_CS]
  _GroupVersion = 1
